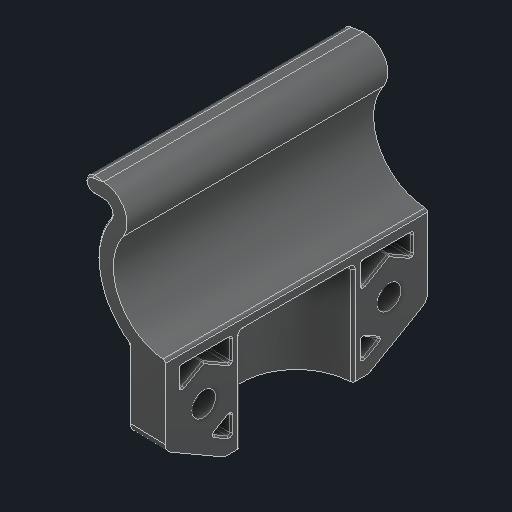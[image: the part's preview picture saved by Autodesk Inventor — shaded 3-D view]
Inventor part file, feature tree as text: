
AUTODESK INVENTOR PART (.ipt)
format: ipt  version: 2024 (Build 280153000, 153)  size: 651,776 bytes
history: native  units: in
note: dims shown in document units (in); Inventor stores cm internally (conversion verified against a paired STEP export)
features: fillet x1
ambient origin geometry x8: Origin, YZ Plane, XZ Plane, XY Plane, X Axis, Y Axis, Z Axis, Center Point
bodies: Solid1 (feature_tree)
feature tree (1):
  fillet  "Fillet15"  [1 undecoded]
note: 1 required parameter value undecoded (feature->parameter linkage not recoverable at this tier; creation-order binding heuristic only, values carry confidence <= 0.55)
